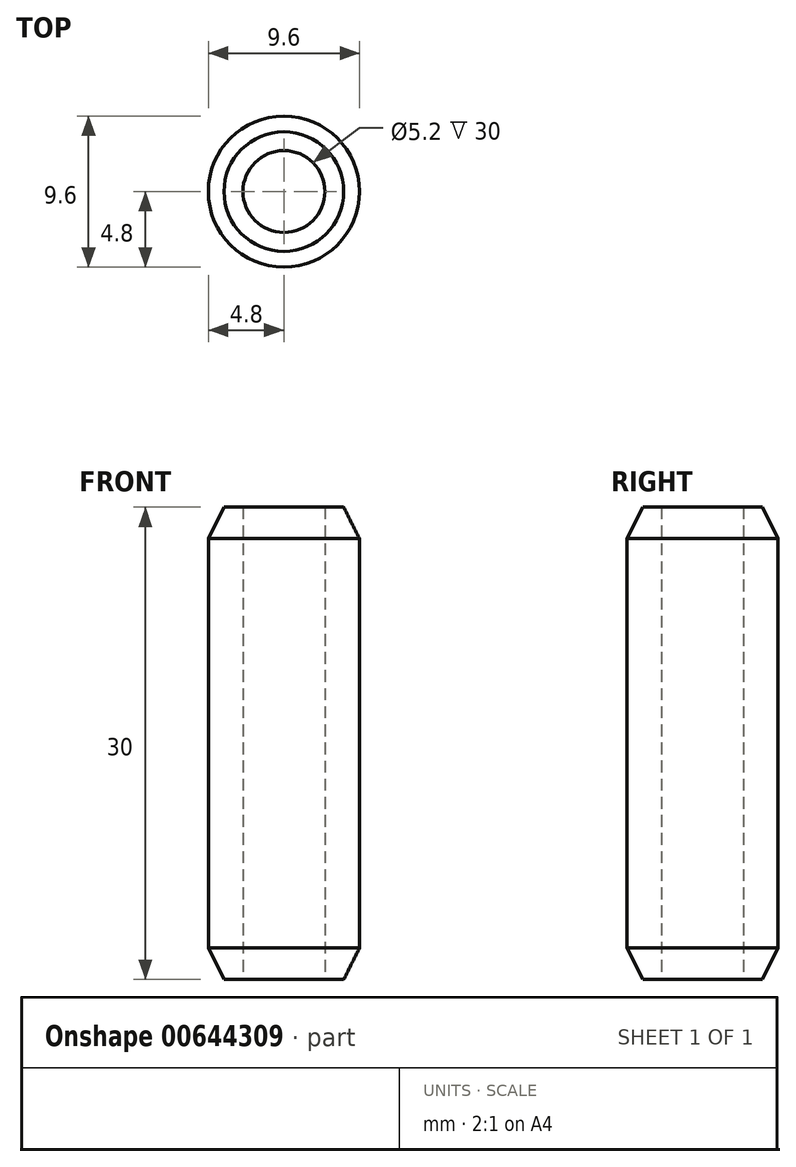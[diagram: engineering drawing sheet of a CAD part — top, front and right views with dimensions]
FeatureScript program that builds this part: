
annotation { "Feature Type Name" : "Feature", "Feature Type Description" : "" }
export const myFeature = defineFeature(function(context is Context, id is Id, definition is map)
    precondition{}
    {
        {
            var Q0;
            Q0=qCreatedBy(makeId("Top.planeOp"),FACE);
            var sketch = newSketch(context, id + "F0", { "sketchPlane" : qUnion([Q0])});
            skCircle(sketch, "E0", {"center": v(0, 0) * mm, "radius": 4.8 * mm});
            skCircle(sketch, "E1", {"center": v(0, 0) * mm, "radius": 2.6 * mm});
            skSolve(sketch);
        }
        {
            var Q0;
            Q0 = qSketchRegion(id + "F0", true);
            extrude(context, id + "F1", {"entities" : qUnion([Q0]), "depth" : 30 * mm, "offsetDistance" : 25 * mm});
        }
        {
            var Q0;
            Q0=makeQuery(id+"F1.opExtrude","CAP_EDGE",EDGE,{"disambiguationData":[OSD([sQuery(id+"F0.wireOp",EDGE,"E0")])],"isStart":true});
            var Q1;
            Q1=makeQuery(id+"F1.opExtrude","CAP_EDGE",EDGE,{"disambiguationData":[OSD([sQuery(id+"F0.wireOp",EDGE,"E0")])],"isStart":false});
            chamfer(context, id + "F2", {"entities" : qUnion([Q0, Q1]), "chamferType" : ChamferType.TWO_OFFSETS, "width1" : 2 * mm, "oppositeDirection" : false, "width2" : 1 * mm, "tangentPropagation" : true});
        }
    });
